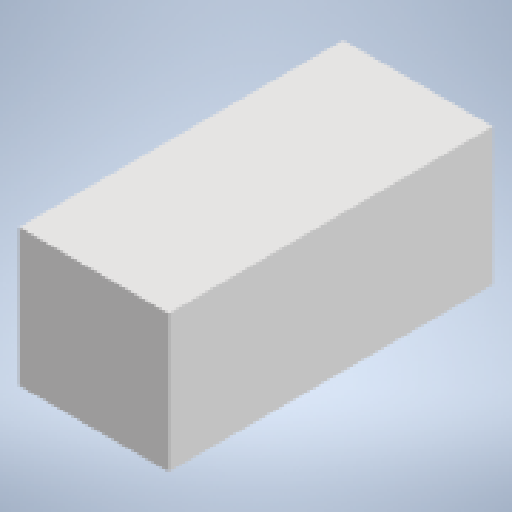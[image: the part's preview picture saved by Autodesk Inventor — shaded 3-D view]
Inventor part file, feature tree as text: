
AUTODESK INVENTOR PART (.ipt)
format: ipt  version: 2023 (Build 270158000, 158)  size: 106,496 bytes
history: native  units: in
note: dims shown in document units (in); Inventor stores cm internally (conversion verified against a paired STEP export)
features: extrude x1, sketch x1
ambient origin geometry x8: Origin, YZ Plane, XZ Plane, XY Plane, X Axis, Y Axis, Z Axis, Center Point
bodies: Solid1 (feature_tree)
feature tree (2):
  extrude  "Extrusion1"  Depth=26.0in
  sketch  "Sketch1"  dims[d0=11.0in d1=26.0in d2=12.0in d3=0.0in]
